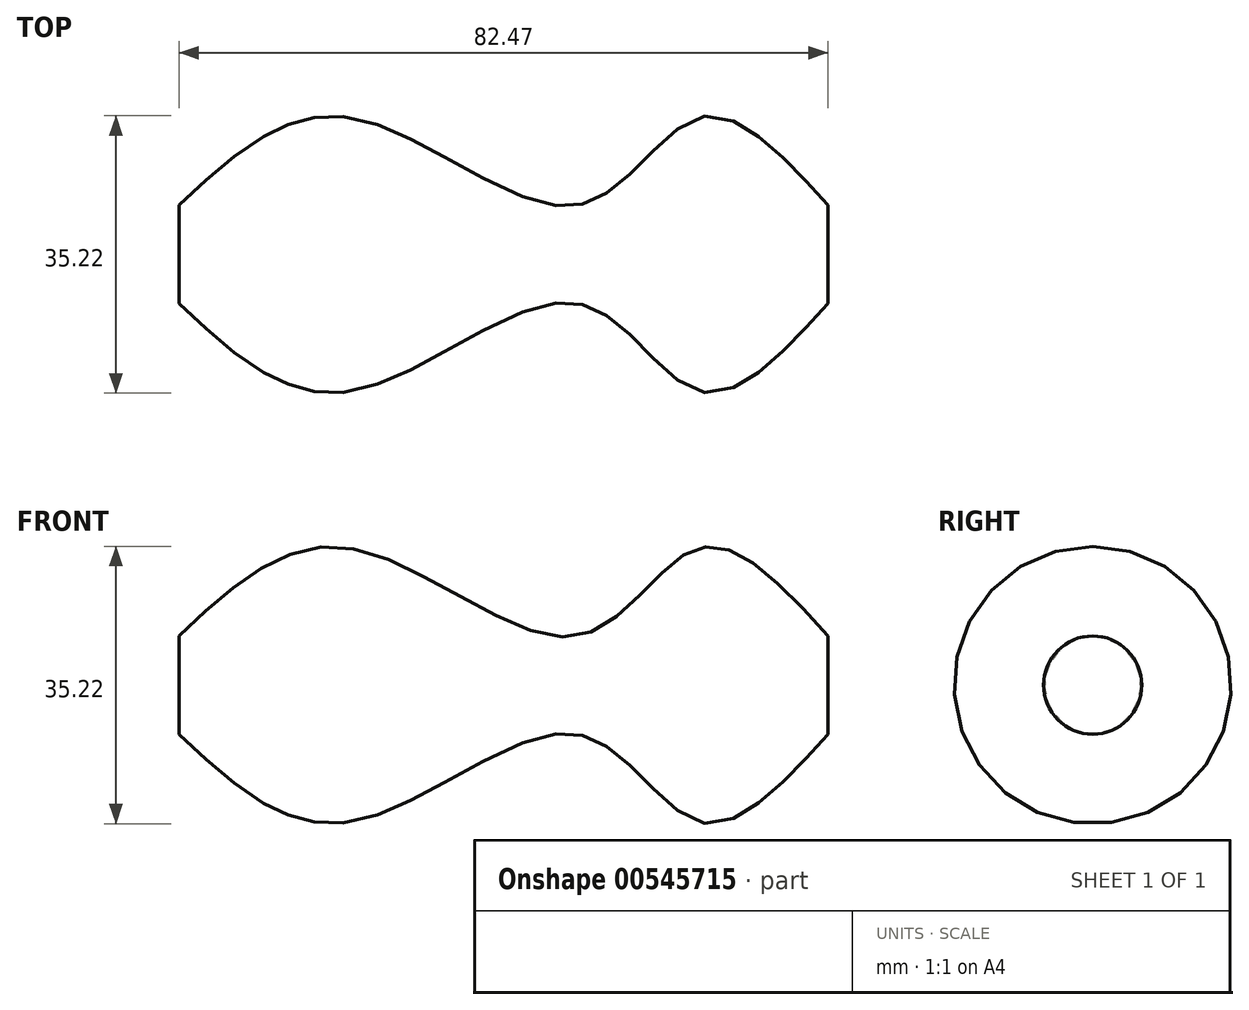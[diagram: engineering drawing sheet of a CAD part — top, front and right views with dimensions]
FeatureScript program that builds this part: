
annotation { "Feature Type Name" : "Feature", "Feature Type Description" : "" }
export const myFeature = defineFeature(function(context is Context, id is Id, definition is map)
    precondition{}
    {
        {
            var Q0;
            Q0=qCreatedBy(makeId("Front.planeOp"),FACE);
            var sketch = newSketch(context, id + "F0", { "sketchPlane" : qUnion([Q0])});
            skLineSegment(sketch, "E0", {"start": v(-50.6, 0) * mm, "end": v(31.87, 0) * mm});
            skLineSegment(sketch, "E1", {"start": v(-50.6, 0) * mm, "end": v(-50.6, 6.24) * mm});
            skLineSegment(sketch, "E2", {"start": v(31.87, 0) * mm, "end": v(31.87, 6.24) * mm});
            skFitSpline(sketch, "E3", {"points": [v(-50.6, 6.24) * mm, v(-28.92, 17.42) * mm, v(0, 6.24) * mm, v(15.44, 17.42) * mm, v(31.87, 6.24) * mm], "startDerivative": vector(78.44, 73.27) * mm, "endDerivative": vector(74.32, -81.74) * mm});
            skSolve(sketch);
        }
        {
            var Q0;
            Q0 = qSketchRegion(id + "F0", true);
            var Q1;
            Q1=sQuery(id+"F0.wireOp",EDGE,"E0");
            revolve(context, id + "F1", {"entities" : qUnion([Q0]), "axis" : qUnion([Q1]), "revolveType" : RevolveType.FULL});
        }
    });
